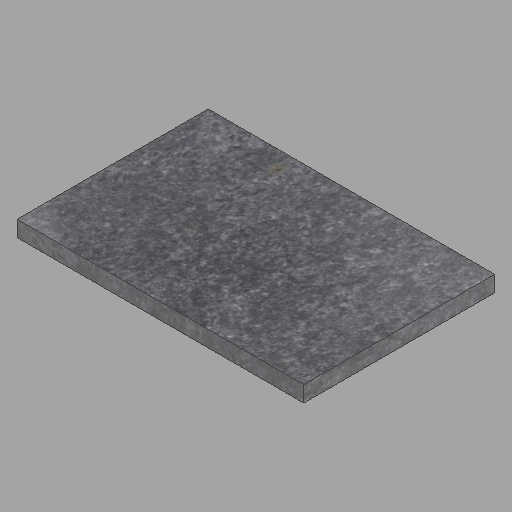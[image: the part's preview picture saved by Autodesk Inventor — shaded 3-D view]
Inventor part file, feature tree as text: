
AUTODESK INVENTOR PART (.ipt)
format: ipt  version: 2023 (Build 270158000, 158)  size: 236,032 bytes
history: native  units: in
note: dims shown in document units (in); Inventor stores cm internally (conversion verified against a paired STEP export)
features: other x1, extrude x1, sketch x1
ambient origin geometry x8: Origin, YZ Plane, XZ Plane, XY Plane, X Axis, Y Axis, Z Axis, Center Point
bodies: Solid1 (feature_tree)
feature tree (3):
  other  "2x24x36-10"
  extrude  "Extrusion1"  Depth=24.0in
  sketch  "Sketch1"  dims[d0=2.0in d1=24.0in d2=36.0in d3=0.0in]
